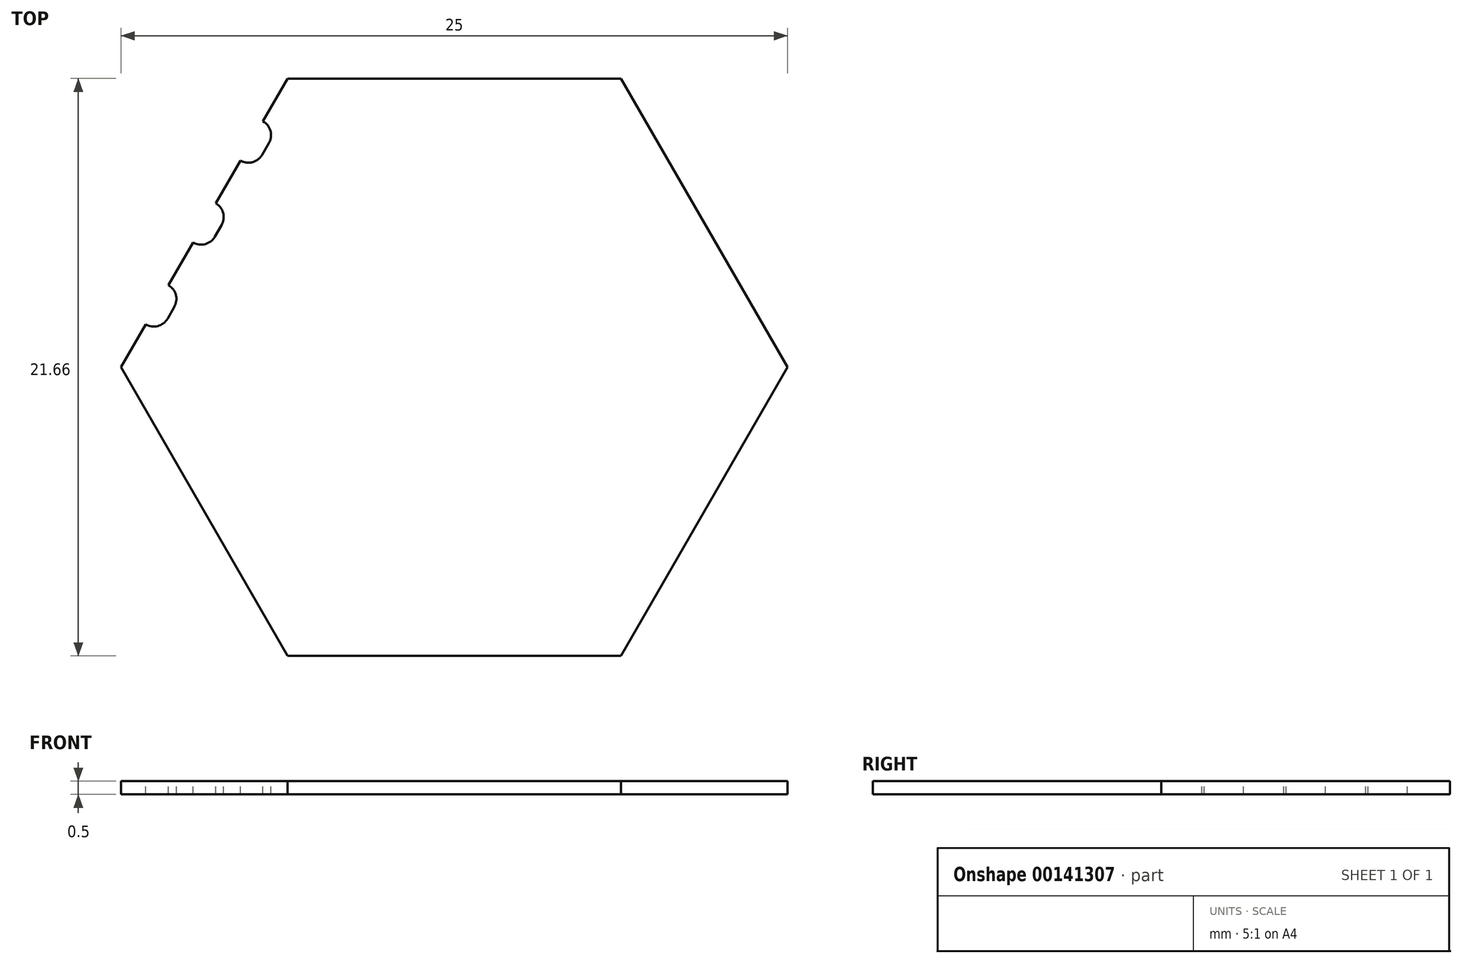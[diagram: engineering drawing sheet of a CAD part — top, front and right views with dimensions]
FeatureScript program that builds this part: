
annotation { "Feature Type Name" : "Feature", "Feature Type Description" : "" }
export const myFeature = defineFeature(function(context is Context, id is Id, definition is map)
    precondition{}
    {
        {
            var Q0;
            Q0=qCreatedBy(makeId("Top.planeOp"),FACE);
            var sketch = newSketch(context, id + "F0", { "sketchPlane" : qUnion([Q0])});
            skCircle(sketch, "E0.cCircle", {"center": v(0, 0) * mm, "radius": 12.5 * mm, "construction": true});
            skLineSegment(sketch, "E0.0", {"start": v(12.5, 0) * mm, "end": v(6.25, -10.83) * mm});
            skLineSegment(sketch, "E0.1", {"start": v(6.25, -10.83) * mm, "end": v(-6.25, -10.83) * mm});
            skLineSegment(sketch, "E0.2", {"start": v(-6.25, -10.83) * mm, "end": v(-12.5, 0) * mm});
            skLineSegment(sketch, "E0.3", {"start": v(-12.5, 0) * mm, "end": v(-6.25, 10.83) * mm});
            skLineSegment(sketch, "E0.4", {"start": v(-6.25, 10.83) * mm, "end": v(6.25, 10.83) * mm});
            skLineSegment(sketch, "E0.5", {"start": v(6.25, 10.83) * mm, "end": v(12.5, 0) * mm});
            skSolve(sketch);
        }
        {
            var Q0;
            Q0=qSketchRegion(id+"F0",true);
            extrude(context, id + "F1", {"entities" : qUnion([Q0]), "depth" : 0.5 * mm});
        }
        {
            var Q0;
            Q0=makeQuery(id+"F1.opExtrude","CAP_FACE",FACE,{"disambiguationData":[OSD([sQuery(id+"F0.wireOp",EDGE,"E0.0"),sQuery(id+"F0.wireOp",EDGE,"E0.1"),sQuery(id+"F0.wireOp",EDGE,"E0.2"),sQuery(id+"F0.wireOp",EDGE,"E0.3"),sQuery(id+"F0.wireOp",EDGE,"E0.4"),sQuery(id+"F0.wireOp",EDGE,"E0.5")])],"isStart":false});
            var sketch = newSketch(context, id + "F2", { "sketchPlane" : qUnion([Q0])});
            skLineSegment(sketch, "E1", {"start": v(3.8, -10.23) * mm, "end": v(3.3, -10.23) * mm});
            skArc(sketch, "E2", {"start": v(3.3, -10.23) * mm, "mid": v(2.88, -10.4) * mm, "end": v(2.7, -10.83) * mm});
            skArc(sketch, "E3", {"start": v(4.4, -10.83) * mm, "mid": v(4.22, -10.4) * mm, "end": v(3.8, -10.23) * mm});
            skLineSegment(sketch, "E4", {"start": v(2.7, -10.83) * mm, "end": v(4.4, -10.83) * mm});
            skPoint(sketch, "E5", {"position": v(-6.25, -10.83) * mm});
            skPoint(sketch, "E6", {"position": v(6.25, -10.83) * mm});
            skLineSegment(sketch, "E7.0", {"start": v(4.4, -10.83) * mm, "end": v(2.7, -10.83) * mm, "construction": true});
            skLineSegment(sketch, "E8", {"start": v(0.25, -10.23) * mm, "end": v(-0.25, -10.23) * mm});
            skArc(sketch, "E9", {"start": v(-0.25, -10.23) * mm, "mid": v(-0.67, -10.4) * mm, "end": v(-0.85, -10.83) * mm});
            skArc(sketch, "E10", {"start": v(0.85, -10.83) * mm, "mid": v(0.67, -10.4) * mm, "end": v(0.25, -10.23) * mm});
            skLineSegment(sketch, "E11", {"start": v(-0.85, -10.83) * mm, "end": v(0.85, -10.83) * mm});
            skLineSegment(sketch, "E12", {"start": v(-3.3, -10.23) * mm, "end": v(-3.8, -10.23) * mm});
            skArc(sketch, "E13", {"start": v(-3.8, -10.23) * mm, "mid": v(-4.22, -10.4) * mm, "end": v(-4.4, -10.83) * mm});
            skArc(sketch, "E14", {"start": v(-2.7, -10.83) * mm, "mid": v(-2.88, -10.4) * mm, "end": v(-3.3, -10.23) * mm});
            skLineSegment(sketch, "E15", {"start": v(-4.4, -10.83) * mm, "end": v(-2.7, -10.83) * mm});
            skLineSegment(sketch, "E16.trimOffspring", {"start": v(0.85, -10.83) * mm, "end": v(-6.25, -10.83) * mm, "construction": true});
            skLineSegment(sketch, "E17", {"start": v(0.85, -10.83) * mm, "end": v(2.7, -10.83) * mm, "construction": true});
            skLineSegment(sketch, "E18", {"start": v(4.4, -10.83) * mm, "end": v(6.25, -10.83) * mm, "construction": true});
            skSolve(sketch);
        }
        {
            var Q0;
            Q0=qSketchRegion(id+"F2",true);
            extrude(context, id + "F3", {"entities" : qUnion([Q0]), "operationType" : NewBodyOperationType.REMOVE, "endBound" : BoundingType.THROUGH_ALL, "oppositeDirection" : true, "depth" : 25 * mm});
        }
        {
            var Q0;
            Q0=qCreatedBy(makeId("Front.planeOp"),FACE);
            var sketch = newSketch(context, id + "F4", { "sketchPlane" : qUnion([Q0])});
            skLineSegment(sketch, "E19", {"start": v(0, -13.24) * mm, "end": v(0, 11.44) * mm, "construction": true});
            skSolve(sketch);
        }
        {
            var Q0;
            Q0=makeQuery(id+"F1.opExtrude","SWEPT_BODY",BODY,{"disambiguationData":[OSD([sQuery(id+"F0.wireOp",EDGE,"E0.0"),sQuery(id+"F0.wireOp",EDGE,"E0.1"),sQuery(id+"F0.wireOp",EDGE,"E0.2"),sQuery(id+"F0.wireOp",EDGE,"E0.3"),sQuery(id+"F0.wireOp",EDGE,"E0.4"),sQuery(id+"F0.wireOp",EDGE,"E0.5")])]});
            var Q1;
            Q1=sQuery(id+"F4.wireOp",EDGE,"E19");
            transform(context, id + "F5", {"entities" : qUnion([Q0]), "transformType" : TransformType.ROTATION, "transformAxis" : qUnion([Q1]), "angle" : 240 * degree, "makeCopy" : false});
        }
    });
